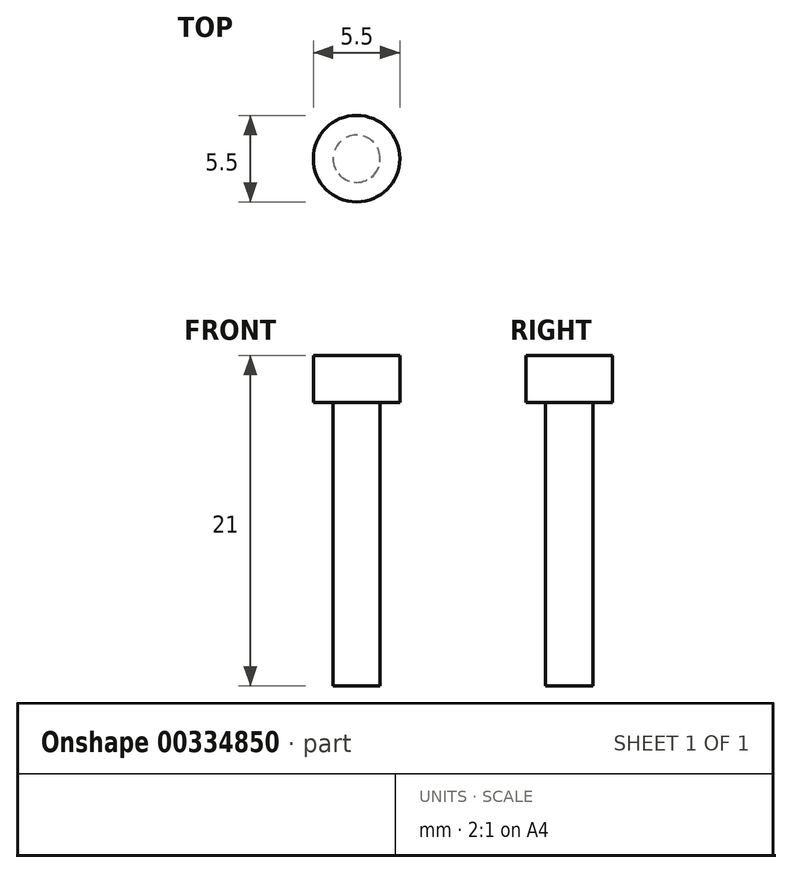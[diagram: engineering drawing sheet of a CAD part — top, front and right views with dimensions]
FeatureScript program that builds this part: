
annotation { "Feature Type Name" : "Feature", "Feature Type Description" : "" }
export const myFeature = defineFeature(function(context is Context, id is Id, definition is map)
    precondition{}
    {
        {
            var Q0;
            Q0=qCreatedBy(makeId("Front.planeOp"),FACE);
            var sketch = newSketch(context, id + "F0", { "sketchPlane" : qUnion([Q0])});
            skLineSegment(sketch, "E0", {"start": v(0, 0) * mm, "end": v(2.75, 0) * mm});
            skLineSegment(sketch, "E1", {"start": v(2.75, 0) * mm, "end": v(2.75, 3) * mm});
            skLineSegment(sketch, "E2", {"start": v(2.75, 3) * mm, "end": v(0, 3) * mm});
            skLineSegment(sketch, "E3", {"start": v(0, 3) * mm, "end": v(0, 0) * mm});
            skSolve(sketch);
        }
        {
            var Q0;
            Q0 = qSketchRegion(id + "F0", true);
            var Q1;
            Q1=sQuery(id+"F0.wireOp",EDGE,"E3");
            revolve(context, id + "F1", {"surfaceOperationType" : NewSurfaceOperationType.NEW, "entities" : qUnion([Q0]), "axis" : qUnion([Q1]), "revolveType" : RevolveType.FULL});
        }
        {
            var Q0;
            Q0=makeQuery(id+"F1.opRevolve","SWEPT_BODY",BODY,{"disambiguationData":[OSD([sQuery(id+"F0.wireOp",EDGE,"E0"),sQuery(id+"F0.wireOp",EDGE,"E1"),sQuery(id+"F0.wireOp",EDGE,"E2"),sQuery(id+"F0.wireOp",EDGE,"E3")])]});
            transform(context, id + "F2", {"entities" : qUnion([Q0]), "transformType" : TransformType.COPY});
        }
        {
            var Q0;
            Q0=makeQuery(id+"F1.opRevolve","SWEPT_FACE",FACE,{"disambiguationData":[OSD([sQuery(id+"F0.wireOp",EDGE,"E0")])]});
            var sketch = newSketch(context, id + "F3", { "sketchPlane" : qUnion([Q0])});
            skCircle(sketch, "E4", {"center": v(0, 0) * mm, "radius": 1.5 * mm});
            skSolve(sketch);
        }
        {
            var Q0;
            Q0 = qSketchRegion(id + "F3", true);
            extrude(context, id + "F4", {"entities" : qUnion([Q0]), "operationType" : NewBodyOperationType.ADD, "depth" : 18 * mm, "offsetDistance" : 25 * mm});
        }
        {
            var Q0;
            Q0 = qSketchRegion(id + "F3", true);
            extrude(context, id + "F5", {"entities" : qUnion([Q0]), "operationType" : NewBodyOperationType.ADD, "depth" : 11 * mm, "offsetDistance" : 25 * mm});
        }
        {
            var Q0;
            Q0=qCreatedBy(makeId("Front.planeOp"),FACE);
            var sketch = newSketch(context, id + "F6", { "sketchPlane" : qUnion([Q0])});
            skLineSegment(sketch, "E5", {"start": v(0, 0) * mm, "end": v(1.9, 0) * mm});
            skLineSegment(sketch, "E6", {"start": v(1.9, 0) * mm, "end": v(1.9, 2) * mm});
            skLineSegment(sketch, "E7", {"start": v(1.9, 2) * mm, "end": v(0, 2) * mm});
            skLineSegment(sketch, "E8", {"start": v(0, 2) * mm, "end": v(0, 0) * mm});
            skSolve(sketch);
        }
        {
            var Q0;
            Q0 = qSketchRegion(id + "F6", true);
            var Q1;
            Q1=sQuery(id+"F6.wireOp",EDGE,"E8");
            revolve(context, id + "F7", {"surfaceOperationType" : NewSurfaceOperationType.NEW, "entities" : qUnion([Q0]), "axis" : qUnion([Q1]), "revolveType" : RevolveType.FULL});
        }
        {
            var Q0;
            Q0=makeQuery(id+"F7.opRevolve","SWEPT_FACE",FACE,{"disambiguationData":[OSD([sQuery(id+"F6.wireOp",EDGE,"E5")])]});
            var sketch = newSketch(context, id + "F8", { "sketchPlane" : qUnion([Q0])});
            skCircle(sketch, "E9", {"center": v(0, 0) * mm, "radius": 1 * mm});
            skSolve(sketch);
        }
        {
            var Q0;
            Q0 = qSketchRegion(id + "F8", true);
            extrude(context, id + "F9", {"entities" : qUnion([Q0]), "operationType" : NewBodyOperationType.ADD, "depth" : 8 * mm, "offsetDistance" : 25 * mm});
        }
    });
